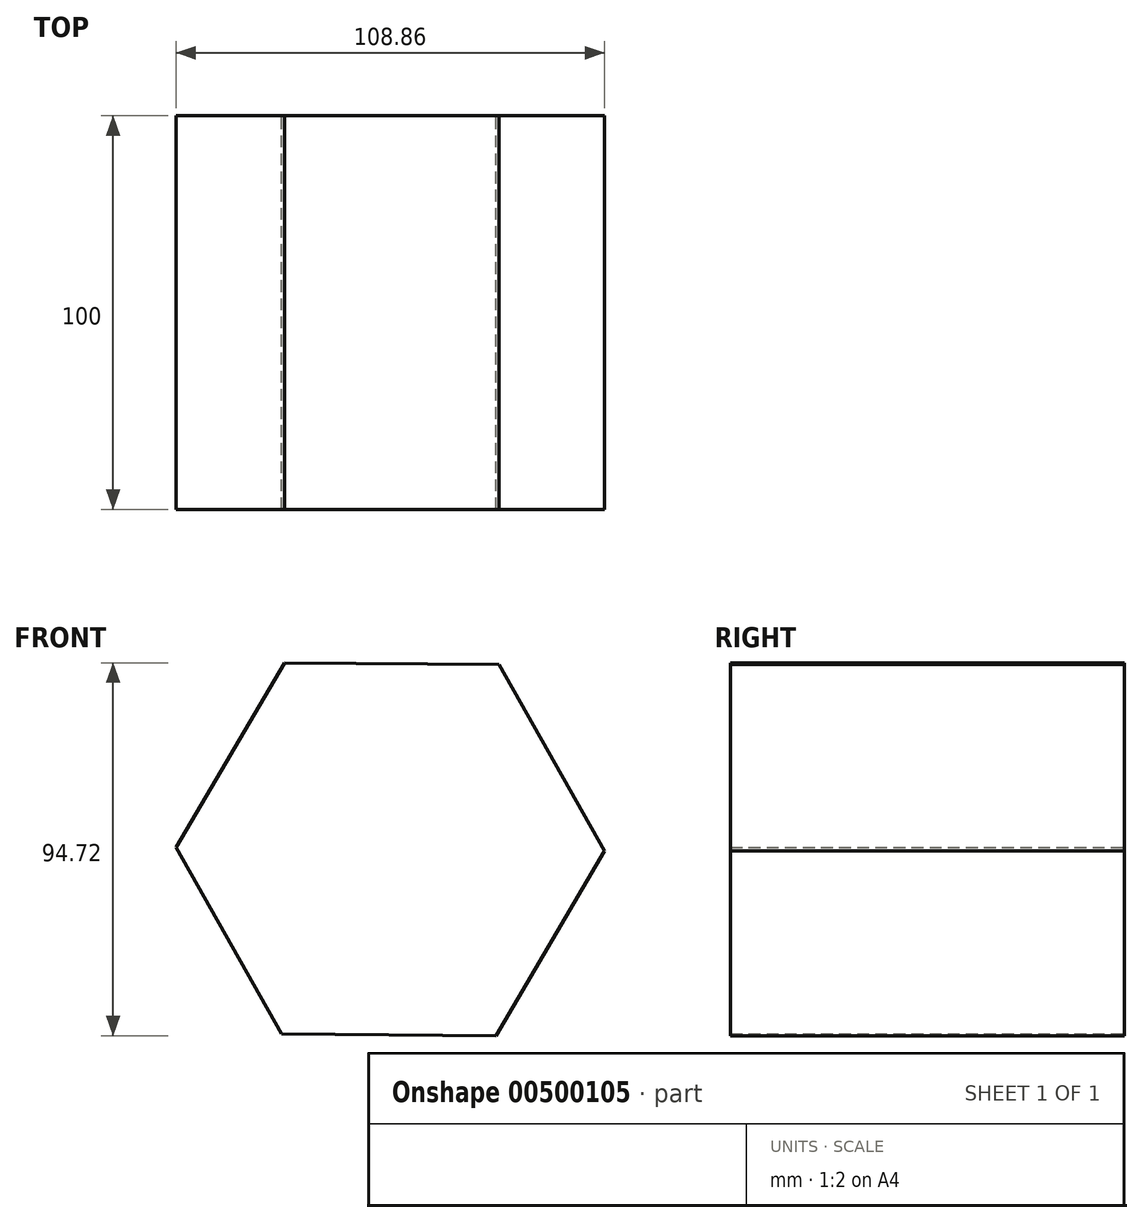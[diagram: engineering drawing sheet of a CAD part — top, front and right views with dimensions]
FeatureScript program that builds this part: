
annotation { "Feature Type Name" : "Feature", "Feature Type Description" : "" }
export const myFeature = defineFeature(function(context is Context, id is Id, definition is map)
    precondition{}
    {
        {
            var Q0;
            Q0=qCreatedBy(makeId("Front.planeOp"),FACE);
            var sketch = newSketch(context, id + "F0", { "sketchPlane" : qUnion([Q0])});
            skCircle(sketch, "E0.cCircle", {"center": v(0, 0) * mm, "radius": 54.43 * mm, "construction": true});
            skLineSegment(sketch, "E0.0", {"start": v(26.82, -47.36) * mm, "end": v(-27.61, -46.9) * mm});
            skLineSegment(sketch, "E0.1", {"start": v(-27.61, -46.9) * mm, "end": v(-54.43, 0.46) * mm});
            skLineSegment(sketch, "E0.2", {"start": v(-54.43, 0.46) * mm, "end": v(-26.82, 47.36) * mm});
            skLineSegment(sketch, "E0.3", {"start": v(-26.82, 47.36) * mm, "end": v(27.61, 46.9) * mm});
            skLineSegment(sketch, "E0.4", {"start": v(27.61, 46.9) * mm, "end": v(54.43, -0.46) * mm});
            skLineSegment(sketch, "E0.5", {"start": v(54.43, -0.46) * mm, "end": v(26.82, -47.36) * mm});
            skSolve(sketch);
        }
        {
            var Q0;
            Q0 = qSketchRegion(id + "F0", true);
            extrude(context, id + "F1", {"entities" : qUnion([Q0]), "endBound" : BoundingType.SYMMETRIC, "depth" : 100 * mm});
        }
    });
